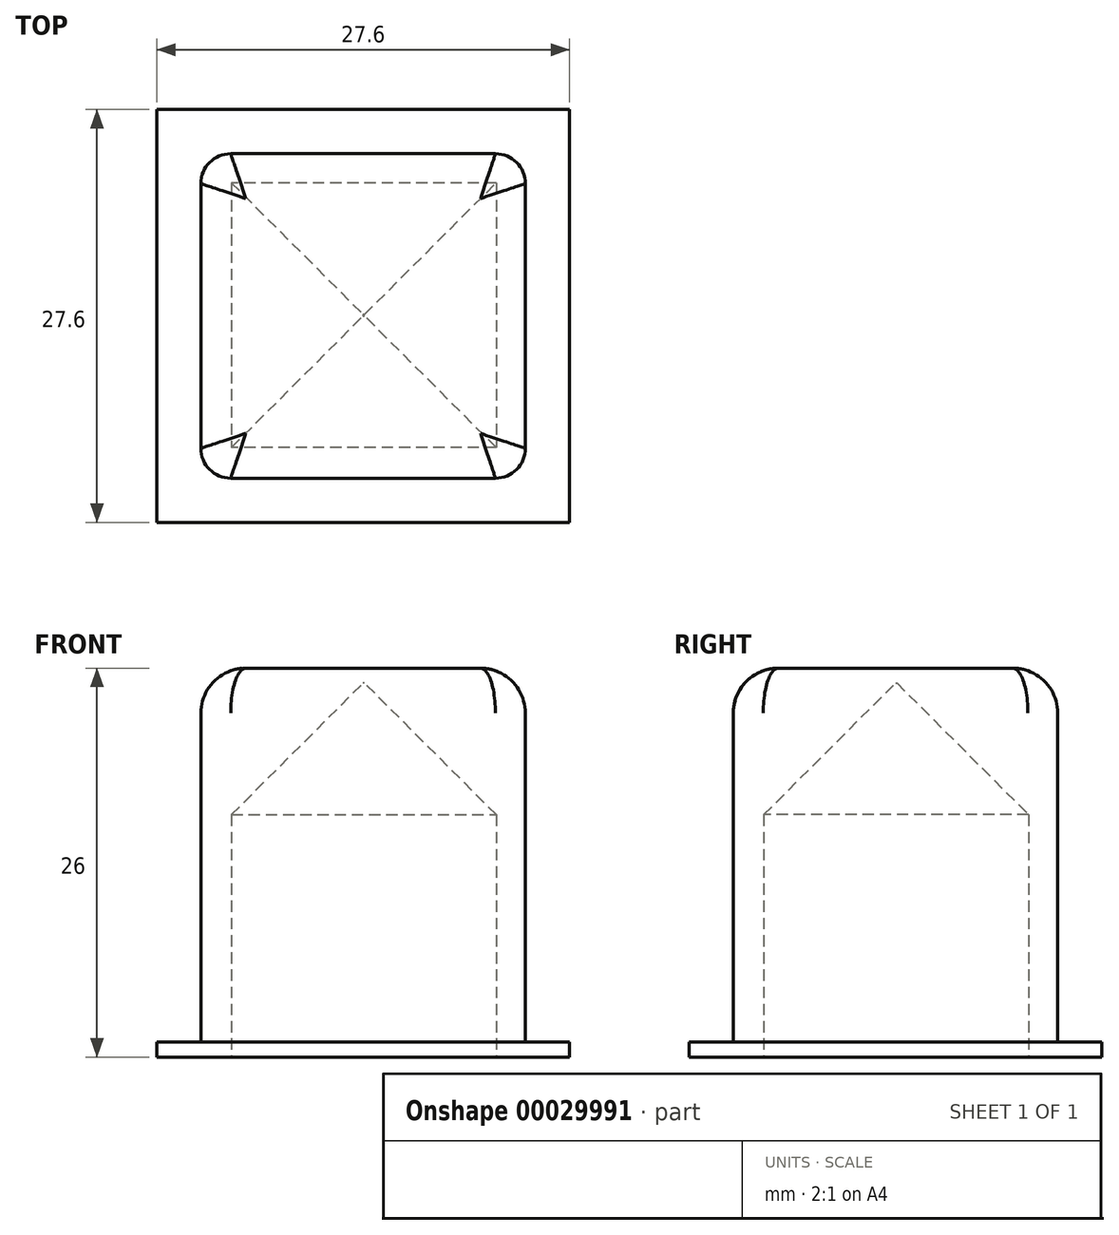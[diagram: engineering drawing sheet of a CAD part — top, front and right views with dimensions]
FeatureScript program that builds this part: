
annotation { "Feature Type Name" : "Feature", "Feature Type Description" : "" }
export const myFeature = defineFeature(function(context is Context, id is Id, definition is map)
    precondition{}
    {
        {
            var Q0;
            Q0=qCreatedBy(makeId("Top.planeOp"),FACE);
            var sketch = newSketch(context, id + "F0", { "sketchPlane" : qUnion([Q0])});
            skLineSegment(sketch, "E0.bottom", {"start": v(0, 0) * mm, "end": v(27.6, 0) * mm});
            skLineSegment(sketch, "E0.top", {"start": v(0, 27.6) * mm, "end": v(27.6, 27.6) * mm});
            skLineSegment(sketch, "E0.left", {"start": v(0, 0) * mm, "end": v(0, 27.6) * mm});
            skLineSegment(sketch, "E0.right", {"start": v(27.6, 0) * mm, "end": v(27.6, 27.6) * mm});
            skSolve(sketch);
        }
        {
            var Q0;
            Q0=makeQuery(id+"F0.imprint","IMPRINT",FACE,{"disambiguationData":[TD([[makeQuery(id+"F0.imprint","IMPRINT",EDGE,{"derivedFrom":sQuery(id+"F0.wireOp",EDGE,"E0.bottom")}),1.0]])]});
            extrude(context, id + "F1", {"entities" : qUnion([Q0]), "depth" : 1 * mm});
        }
        {
            var Q0;
            Q0=makeQuery(id+"F1.opExtrude","CAP_FACE",FACE,{"disambiguationData":[OSD([sQuery(id+"F0.wireOp",EDGE,"E0.bottom"),sQuery(id+"F0.wireOp",EDGE,"E0.top"),sQuery(id+"F0.wireOp",EDGE,"E0.left"),sQuery(id+"F0.wireOp",EDGE,"E0.right")])],"isStart":false});
            var sketch = newSketch(context, id + "F2", { "sketchPlane" : qUnion([Q0])});
            skLineSegment(sketch, "E1", {"start": v(13.8, 27.6) * mm, "end": v(13.8, 0) * mm, "construction": true});
            skLineSegment(sketch, "E2.rect.bottom", {"start": v(24.65, 2.95) * mm, "end": v(2.95, 2.95) * mm});
            skLineSegment(sketch, "E2.rect.top", {"start": v(24.65, 24.65) * mm, "end": v(2.95, 24.65) * mm});
            skLineSegment(sketch, "E2.rect.left", {"start": v(24.65, 2.95) * mm, "end": v(24.65, 24.65) * mm});
            skLineSegment(sketch, "E2.rect.right", {"start": v(2.95, 2.95) * mm, "end": v(2.95, 24.65) * mm});
            skPoint(sketch, "E2.rect.middle", {"position": v(13.8, 13.8) * mm});
            skSolve(sketch);
        }
        {
            var Q0;
            Q0=makeQuery(id+"F2.imprint","IMPRINT",FACE,{"disambiguationData":[TD([[makeQuery(id+"F2.imprint","IMPRINT",EDGE,{"derivedFrom":sQuery(id+"F2.wireOp",EDGE,"E2.rect.bottom")}),-1.0]])]});
            extrude(context, id + "F3", {"entities" : qUnion([Q0]), "operationType" : NewBodyOperationType.ADD, "depth" : 25 * mm});
        }
        {
            var Q0;
            Q0=makeQuery(id+"F3.opExtrude","CAP_EDGE",EDGE,{"disambiguationData":[OSD([sQuery(id+"F2.wireOp",EDGE,"E2.rect.left")])],"isStart":false});
            var Q1;
            Q1=makeQuery(id+"F3.opExtrude","CAP_EDGE",EDGE,{"disambiguationData":[OSD([sQuery(id+"F2.wireOp",EDGE,"E2.rect.bottom")])],"isStart":false});
            var Q2;
            Q2=makeQuery(id+"F3.opExtrude","CAP_EDGE",EDGE,{"disambiguationData":[OSD([sQuery(id+"F2.wireOp",EDGE,"E2.rect.right")])],"isStart":false});
            var Q3;
            Q3=makeQuery(id+"F3.opExtrude","CAP_EDGE",EDGE,{"disambiguationData":[OSD([sQuery(id+"F2.wireOp",EDGE,"E2.rect.top")])],"isStart":false});
            fillet(context, id + "F4", {"entities" : qUnion([Q0, Q1, Q2, Q3]), "radius" : 3 * mm, "tangentPropagation" : true, "allowEdgeOverflow" : false});
        }
        {
            var Q0;
            Q0=makeQuery(id+"F3.opExtrude","SWEPT_EDGE",EDGE,{"disambiguationData":[OSD([sQuery(id+"F2.wireOp",EDGE,"E2.rect.bottom"),sQuery(id+"F2.wireOp",EDGE,"E2.rect.left")])]});
            var Q1;
            Q1=makeQuery(id+"F3.opExtrude","SWEPT_EDGE",EDGE,{"disambiguationData":[OSD([sQuery(id+"F2.wireOp",EDGE,"E2.rect.top"),sQuery(id+"F2.wireOp",EDGE,"E2.rect.left")])]});
            var Q2;
            Q2=makeQuery(id+"F3.opExtrude","SWEPT_EDGE",EDGE,{"disambiguationData":[OSD([sQuery(id+"F2.wireOp",EDGE,"E2.rect.bottom"),sQuery(id+"F2.wireOp",EDGE,"E2.rect.right")])]});
            var Q3;
            Q3=makeQuery(id+"F3.opExtrude","CAP_EDGE",EDGE,{"disambiguationData":[OSD([sQuery(id+"F2.wireOp",EDGE,"E2.rect.left")])],"isStart":true});
            var Q4;
            Q4=makeQuery(id+"F3.opExtrude","SWEPT_EDGE",EDGE,{"disambiguationData":[OSD([sQuery(id+"F2.wireOp",EDGE,"E2.rect.top"),sQuery(id+"F2.wireOp",EDGE,"E2.rect.right")])]});
            fillet(context, id + "F5", {"entities" : qUnion([Q0, Q1, Q2, Q3, Q4]), "radius" : 2 * mm, "tangentPropagation" : true, "allowEdgeOverflow" : false});
        }
        {
            var Q0;
            Q0=qCreatedBy(makeId("Top.planeOp"),FACE);
            var sketch = newSketch(context, id + "F6", { "sketchPlane" : qUnion([Q0])});
            skLineSegment(sketch, "E3.bottom", {"start": v(0, 0) * mm, "end": v(27.7, 0) * mm, "construction": true});
            skLineSegment(sketch, "E3.top", {"start": v(0, 27.7) * mm, "end": v(27.7, 27.7) * mm, "construction": true});
            skLineSegment(sketch, "E3.left", {"start": v(0, 0) * mm, "end": v(0, 27.7) * mm, "construction": true});
            skLineSegment(sketch, "E3.right", {"start": v(27.7, 0) * mm, "end": v(27.7, 27.7) * mm, "construction": true});
            skLineSegment(sketch, "E4", {"start": v(0, 13.85) * mm, "end": v(27.7, 13.85) * mm, "construction": true});
            skLineSegment(sketch, "E5.rect.bottom", {"start": v(22.7, 22.7) * mm, "end": v(5, 22.7) * mm});
            skLineSegment(sketch, "E5.rect.top", {"start": v(22.7, 5) * mm, "end": v(5, 5) * mm});
            skLineSegment(sketch, "E5.rect.left", {"start": v(22.7, 22.7) * mm, "end": v(22.7, 5) * mm});
            skLineSegment(sketch, "E5.rect.right", {"start": v(5, 22.7) * mm, "end": v(5, 5) * mm});
            skPoint(sketch, "E5.rect.middle", {"position": v(13.85, 13.85) * mm});
            skSolve(sketch);
        }
        {
            var Q0;
            Q0=makeQuery(id+"F6.imprint","IMPRINT",FACE,{"disambiguationData":[TD([[makeQuery(id+"F6.imprint","IMPRINT",EDGE,{"derivedFrom":sQuery(id+"F6.wireOp",EDGE,"E5.rect.bottom")}),1.0]])]});
            extrude(context, id + "F7", {"entities" : qUnion([Q0]), "depth" : 25 * mm});
        }
        {
            var Q0;
            Q0=makeQuery(id+"F7.opExtrude","CAP_EDGE",EDGE,{"disambiguationData":[OSD([sQuery(id+"F6.wireOp",EDGE,"E5.rect.right")])],"isStart":false});
            var Q1;
            Q1=makeQuery(id+"F7.opExtrude","CAP_EDGE",EDGE,{"disambiguationData":[OSD([sQuery(id+"F6.wireOp",EDGE,"E5.rect.top")])],"isStart":false});
            var Q2;
            Q2=makeQuery(id+"F7.opExtrude","CAP_EDGE",EDGE,{"disambiguationData":[OSD([sQuery(id+"F6.wireOp",EDGE,"E5.rect.left")])],"isStart":false});
            var Q3;
            Q3=makeQuery(id+"F7.opExtrude","CAP_EDGE",EDGE,{"disambiguationData":[OSD([sQuery(id+"F6.wireOp",EDGE,"E5.rect.bottom")])],"isStart":false});
            chamfer(context, id + "F8", {"entities" : qUnion([Q0, Q1, Q2, Q3]), "width" : 8.8 * mm, "tangentPropagation" : true});
        }
        {
            var Q0;
            Q0=makeQuery(id+"F7.opExtrude","SWEPT_BODY",BODY,{"disambiguationData":[OSD([sQuery(id+"F6.wireOp",EDGE,"E5.rect.bottom"),sQuery(id+"F6.wireOp",EDGE,"E5.rect.top"),sQuery(id+"F6.wireOp",EDGE,"E5.rect.left"),sQuery(id+"F6.wireOp",EDGE,"E5.rect.right")])]});
            var Q1;
            Q1=makeQuery(id+"F1.opExtrude","SWEPT_BODY",BODY,{"disambiguationData":[OSD([sQuery(id+"F0.wireOp",EDGE,"E0.bottom"),sQuery(id+"F0.wireOp",EDGE,"E0.top"),sQuery(id+"F0.wireOp",EDGE,"E0.left"),sQuery(id+"F0.wireOp",EDGE,"E0.right")])]});
            booleanBodies(context, id + "F9", {"operationType" : BooleanOperationType.SUBTRACTION, "tools" : qUnion([Q0]), "targets" : qUnion([Q1])});
        }
    });
